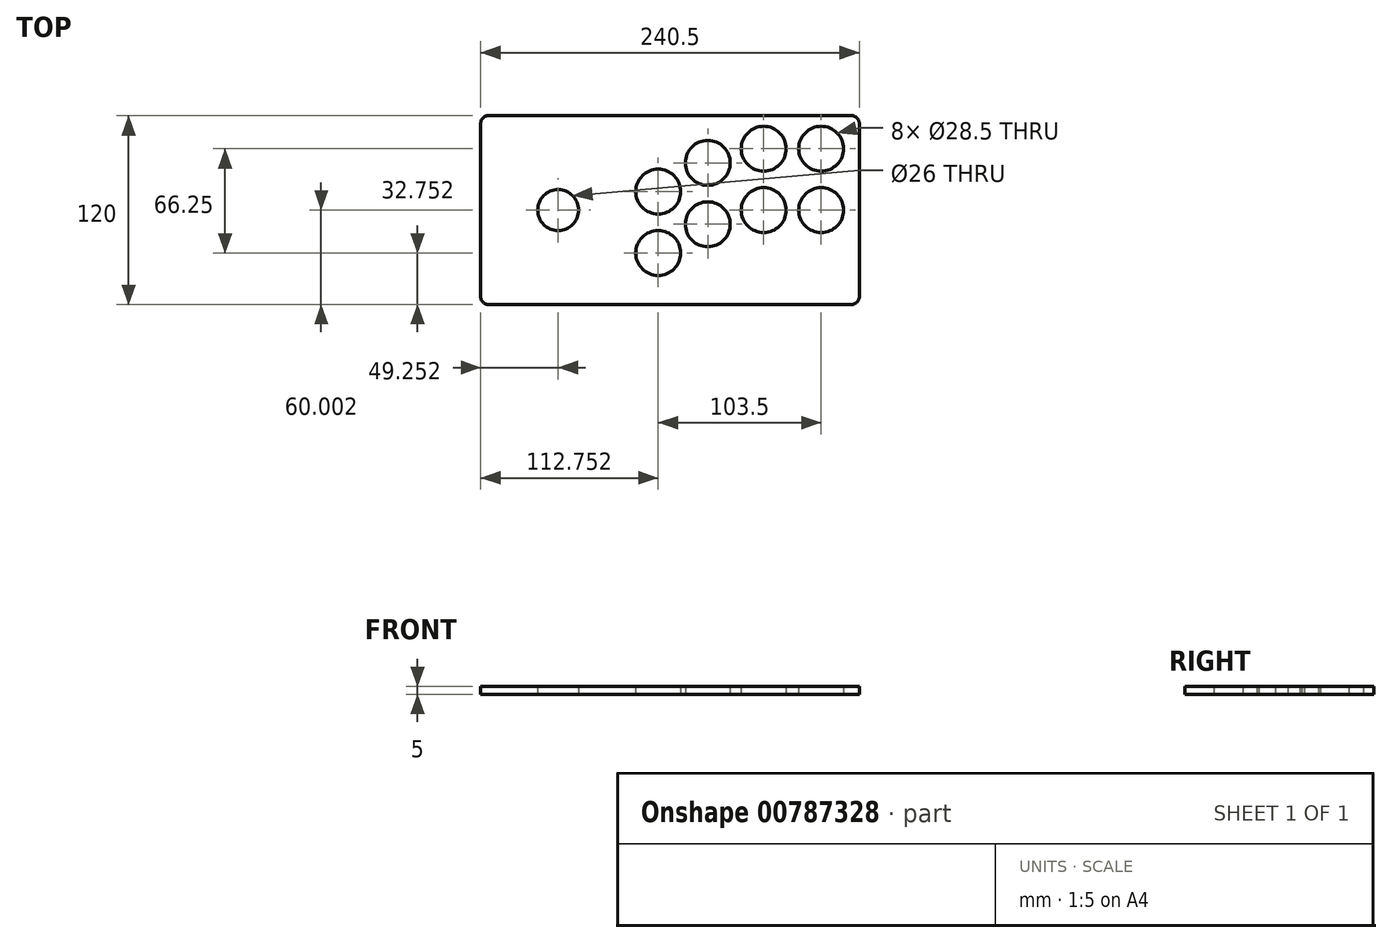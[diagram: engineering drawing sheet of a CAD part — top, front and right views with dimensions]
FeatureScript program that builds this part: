
annotation { "Feature Type Name" : "Feature", "Feature Type Description" : "" }
export const myFeature = defineFeature(function(context is Context, id is Id, definition is map)
    precondition{}
    {
        {
            var Q0;
            Q0=qCreatedBy(makeId("Top.planeOp"),FACE);
            var sketch = newSketch(context, id + "F0", { "sketchPlane" : qUnion([Q0])});
            skPoint(sketch, "E0.middle", {"position": v(0, 0) * mm});
            skLineSegment(sketch, "E1", {"start": v(-94.85, -31.6) * mm, "end": v(0.15, -31.6) * mm, "construction": true});
            skLineSegment(sketch, "E2", {"start": v(0.15, -31.6) * mm, "end": v(31.65, -31.6) * mm, "construction": true});
            skLineSegment(sketch, "E3", {"start": v(31.65, -31.6) * mm, "end": v(67.15, -31.6) * mm, "construction": true});
            skLineSegment(sketch, "E4", {"start": v(67.15, -31.6) * mm, "end": v(103.65, -31.6) * mm, "construction": true});
            skLineSegment(sketch, "E5", {"start": v(-58.37, 34.65) * mm, "end": v(-58.37, 25.65) * mm, "construction": true});
            skLineSegment(sketch, "E6", {"start": v(-58.37, 25.65) * mm, "end": v(-58.37, 7.4) * mm, "construction": true});
            skLineSegment(sketch, "E7", {"start": v(-58.37, 7.4) * mm, "end": v(-58.37, -4.35) * mm, "construction": true});
            skLineSegment(sketch, "E8", {"start": v(-58.37, -4.35) * mm, "end": v(-58.37, -13.35) * mm, "construction": true});
            skLineSegment(sketch, "E9", {"start": v(-58.37, -13.35) * mm, "end": v(-58.37, -31.6) * mm, "construction": true});
            skLineSegment(sketch, "E10", {"start": v(-58.37, -13.35) * mm, "end": v(0.15, -13.35) * mm, "construction": true});
            skLineSegment(sketch, "E11", {"start": v(0.15, -13.35) * mm, "end": v(31.65, -13.35) * mm, "construction": true});
            skLineSegment(sketch, "E12", {"start": v(31.65, -13.35) * mm, "end": v(67.15, -13.35) * mm, "construction": true});
            skLineSegment(sketch, "E13", {"start": v(67.15, -13.35) * mm, "end": v(103.65, -13.35) * mm, "construction": true});
            skLineSegment(sketch, "E14", {"start": v(-58.37, -4.35) * mm, "end": v(0.15, -4.35) * mm, "construction": true});
            skLineSegment(sketch, "E15", {"start": v(0.15, -4.35) * mm, "end": v(31.65, -4.35) * mm, "construction": true});
            skLineSegment(sketch, "E16", {"start": v(31.65, -4.35) * mm, "end": v(67.15, -4.35) * mm, "construction": true});
            skLineSegment(sketch, "E17", {"start": v(67.15, -4.35) * mm, "end": v(103.65, -4.35) * mm, "construction": true});
            skLineSegment(sketch, "E18", {"start": v(-58.37, 7.4) * mm, "end": v(0.15, 7.4) * mm, "construction": true});
            skLineSegment(sketch, "E19", {"start": v(0.15, 7.4) * mm, "end": v(31.65, 7.4) * mm, "construction": true});
            skLineSegment(sketch, "E20", {"start": v(31.65, 7.4) * mm, "end": v(67.15, 7.4) * mm, "construction": true});
            skLineSegment(sketch, "E21", {"start": v(67.15, 7.4) * mm, "end": v(103.65, 7.4) * mm, "construction": true});
            skLineSegment(sketch, "E22", {"start": v(-58.37, 25.65) * mm, "end": v(0.15, 25.65) * mm, "construction": true});
            skLineSegment(sketch, "E23", {"start": v(0.15, 25.65) * mm, "end": v(31.65, 25.65) * mm, "construction": true});
            skLineSegment(sketch, "E24", {"start": v(31.65, 25.65) * mm, "end": v(67.15, 25.65) * mm, "construction": true});
            skLineSegment(sketch, "E25", {"start": v(67.15, 25.65) * mm, "end": v(103.65, 25.65) * mm, "construction": true});
            skLineSegment(sketch, "E26", {"start": v(-58.37, 34.65) * mm, "end": v(0.15, 34.65) * mm, "construction": true});
            skLineSegment(sketch, "E27", {"start": v(0.15, 34.65) * mm, "end": v(31.65, 34.65) * mm, "construction": true});
            skLineSegment(sketch, "E28", {"start": v(31.65, 34.65) * mm, "end": v(67.15, 34.65) * mm, "construction": true});
            skLineSegment(sketch, "E29", {"start": v(67.15, 34.65) * mm, "end": v(103.65, 34.65) * mm, "construction": true});
            skCircle(sketch, "E30", {"center": v(0.15, -31.6) * mm, "radius": 14.25 * mm});
            skCircle(sketch, "E31", {"center": v(0.15, 7.4) * mm, "radius": 14.25 * mm});
            skCircle(sketch, "E32", {"center": v(31.65, 25.65) * mm, "radius": 14.25 * mm});
            skCircle(sketch, "E33", {"center": v(67.15, 34.65) * mm, "radius": 14.25 * mm});
            skCircle(sketch, "E34", {"center": v(103.65, 34.65) * mm, "radius": 14.25 * mm});
            skCircle(sketch, "E35", {"center": v(31.65, -13.35) * mm, "radius": 14.25 * mm});
            skCircle(sketch, "E36", {"center": v(67.15, -4.35) * mm, "radius": 14.25 * mm});
            skCircle(sketch, "E37", {"center": v(103.65, -4.35) * mm, "radius": 14.25 * mm});
            skLineSegment(sketch, "E38", {"start": v(31.65, 34.65) * mm, "end": v(31.65, 54.64) * mm, "construction": true});
            skLineSegment(sketch, "E39", {"start": v(31.65, 54.64) * mm, "end": v(-27.35, 54.64) * mm, "construction": true});
            skLineSegment(sketch, "E40", {"start": v(-27.35, 54.64) * mm, "end": v(-63.35, 54.64) * mm, "construction": true});
            skLineSegment(sketch, "E41", {"start": v(-63.35, 54.64) * mm, "end": v(-63.35, -4.35) * mm, "construction": true});
            skLineSegment(sketch, "E42", {"start": v(-63.35, -4.35) * mm, "end": v(-58.37, -4.35) * mm, "construction": true});
            skCircle(sketch, "E43", {"center": v(-63.35, -4.35) * mm, "radius": 13 * mm});
            skLineSegment(sketch, "E44", {"start": v(-14.1, 7.4) * mm, "end": v(-14.1, -64.35) * mm, "construction": true});
            skLineSegment(sketch, "E45", {"start": v(-14.1, -64.35) * mm, "end": v(-50.67, -64.35) * mm, "construction": true});
            skLineSegment(sketch, "E46", {"start": v(-76.03, -64.35) * mm, "end": v(-50.67, -64.35) * mm, "construction": true});
            skLineSegment(sketch, "E47", {"start": v(-76.03, -64.35) * mm, "end": v(-112.6, -64.35) * mm, "construction": true});
            skLineSegment(sketch, "E48", {"start": v(-112.6, -64.35) * mm, "end": v(-112.6, -4.35) * mm, "construction": true});
            skLineSegment(sketch, "E49", {"start": v(-112.6, -4.35) * mm, "end": v(-76.35, -4.35) * mm, "construction": true});
            skLineSegment(sketch, "E50", {"start": v(-112.6, -4.35) * mm, "end": v(-112.6, 55.65) * mm, "construction": true});
            skLineSegment(sketch, "E51.bottom", {"start": v(-112.6, 55.65) * mm, "end": v(127.9, 55.65) * mm});
            skLineSegment(sketch, "E51.top", {"start": v(-112.6, -64.35) * mm, "end": v(127.9, -64.35) * mm});
            skLineSegment(sketch, "E51.left", {"start": v(-112.6, 55.65) * mm, "end": v(-112.6, -64.35) * mm});
            skLineSegment(sketch, "E51.right", {"start": v(127.9, 55.65) * mm, "end": v(127.9, -64.35) * mm});
            skLineSegment(sketch, "E52", {"start": v(103.65, 34.65) * mm, "end": v(117.9, 34.65) * mm, "construction": true});
            skLineSegment(sketch, "E53", {"start": v(117.9, 34.65) * mm, "end": v(127.9, 34.65) * mm, "construction": true});
            skSolve(sketch);
        }
        {
            var Q0;
            Q0=makeQuery(id+"F0.imprint","IMPRINT",FACE,{"disambiguationData":[TD([[makeQuery(id+"F0.imprint","IMPRINT",EDGE,{"derivedFrom":sQuery(id+"F0.wireOp",EDGE,"E30")}),-1.0]])]});
            extrude(context, id + "F1", {"entities" : qUnion([Q0]), "depth" : 5 * mm, "offsetDistance" : 25 * mm});
        }
        {
            var Q0;
            Q0=makeQuery(id+"F1.opExtrude","SWEPT_EDGE",EDGE,{"disambiguationData":[OSD([sQuery(id+"F0.wireOp",EDGE,"E51.top"),sQuery(id+"F0.wireOp",EDGE,"E51.left")])]});
            var Q1;
            Q1=makeQuery(id+"F1.opExtrude","SWEPT_EDGE",EDGE,{"disambiguationData":[OSD([sQuery(id+"F0.wireOp",EDGE,"E51.top"),sQuery(id+"F0.wireOp",EDGE,"E51.right")])]});
            var Q2;
            Q2=makeQuery(id+"F1.opExtrude","SWEPT_EDGE",EDGE,{"disambiguationData":[OSD([sQuery(id+"F0.wireOp",EDGE,"E51.bottom"),sQuery(id+"F0.wireOp",EDGE,"E51.right")])]});
            var Q3;
            Q3=makeQuery(id+"F1.opExtrude","SWEPT_EDGE",EDGE,{"disambiguationData":[OSD([sQuery(id+"F0.wireOp",EDGE,"E51.bottom"),sQuery(id+"F0.wireOp",EDGE,"E51.left")])]});
            fillet(context, id + "F2", {"entities" : qUnion([Q0, Q1, Q2, Q3]), "radius" : 5 * mm, "tangentPropagation" : true, "allowEdgeOverflow" : false});
        }
    });
